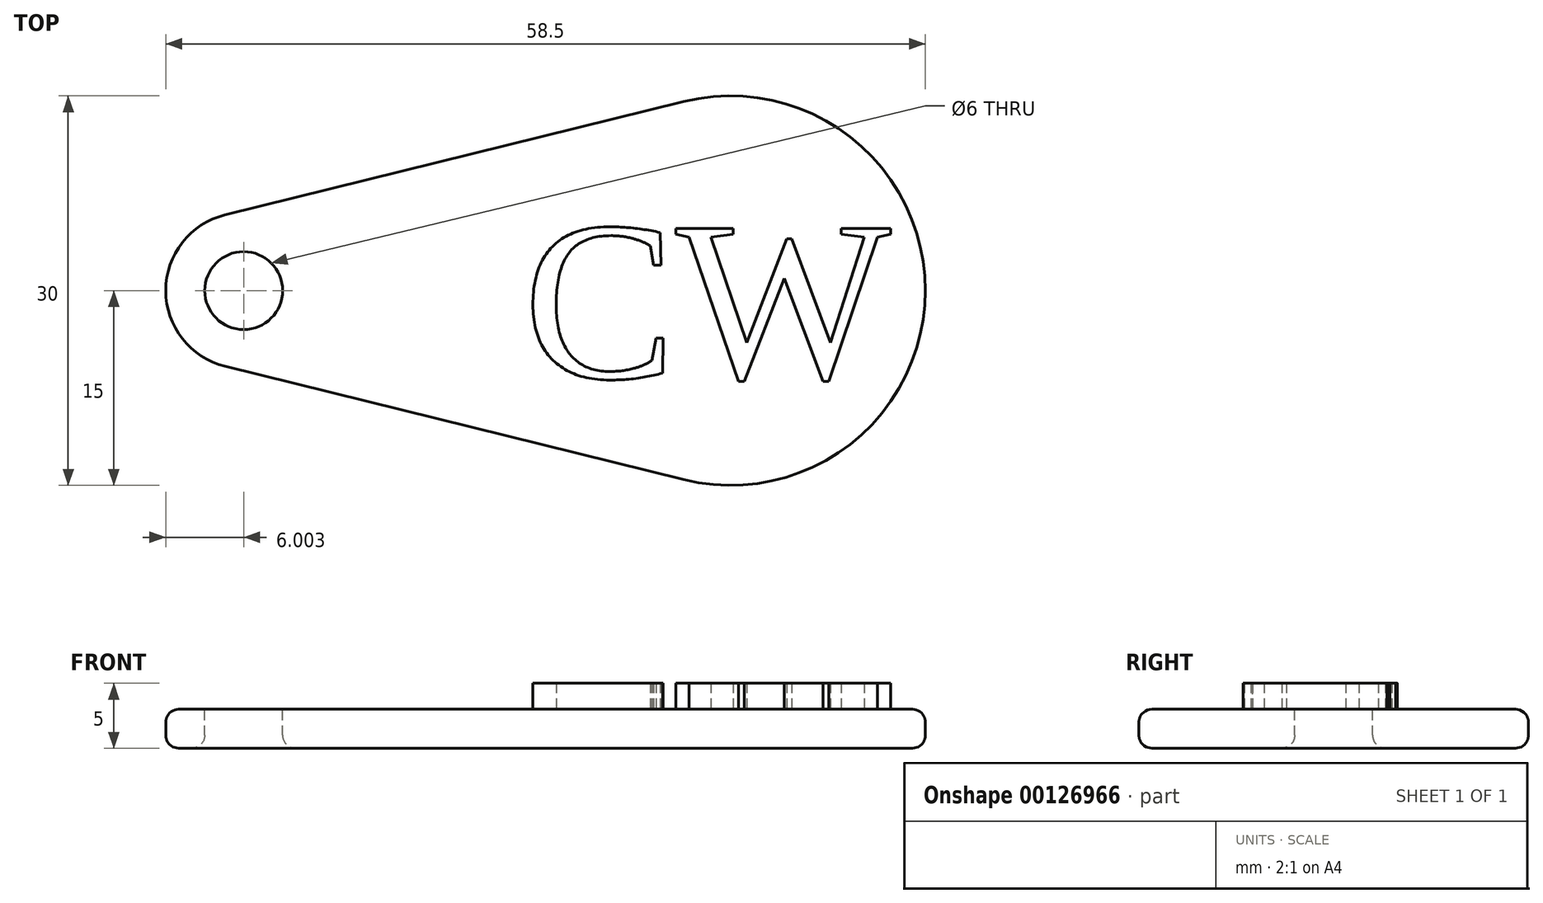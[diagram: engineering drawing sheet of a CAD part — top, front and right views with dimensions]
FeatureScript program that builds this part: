
annotation { "Feature Type Name" : "Feature", "Feature Type Description" : "" }
export const myFeature = defineFeature(function(context is Context, id is Id, definition is map)
    precondition{}
    {
        {
            var Q0;
            Q0=qCreatedBy(makeId("Top.planeOp"),FACE);
            var sketch = newSketch(context, id + "F0", { "sketchPlane" : qUnion([Q0])});
            skCircle(sketch, "E0", {"center": v(46.46, 0) * mm, "radius": 15 * mm});
            skCircle(sketch, "E1", {"center": v(8.96, 0) * mm, "radius": 6 * mm});
            skLineSegment(sketch, "E2", {"start": v(7.52, 5.82) * mm, "end": v(42.86, 14.56) * mm});
            skLineSegment(sketch, "E3", {"start": v(7.52, -5.82) * mm, "end": v(42.86, -14.56) * mm});
            skSolve(sketch);
        }
        {
            var Q0;
            {var subQ0=sQuery(id+"F0.wireOp",EDGE,"E1");var subQ1=makeQuery(id+"F0.imprint","INTERSECT",VERTEX,{"derivedFrom":[subQ0,sQuery(id+"F0.wireOp",EDGE,"E2")]});Q0=makeQuery(id+"F0.imprint","IMPRINT",FACE,{"disambiguationData":[TD([[makeQuery(id+"F0.imprint","IMPRINT",EDGE,{"disambiguationData":[TD([[subQ1,-1.0]])],"derivedFrom":subQ0}),1.0]])]});}
            var Q1;
            {var subQ0=sQuery(id+"F0.wireOp",EDGE,"E2");Q1=makeQuery(id+"F0.imprint","IMPRINT",FACE,{"disambiguationData":[TD([[makeQuery(id+"F0.imprint","IMPRINT",EDGE,{"derivedFrom":subQ0}),-1.0]])]});}
            var Q2;
            {var subQ0=sQuery(id+"F0.wireOp",EDGE,"E0");var subQ1=makeQuery(id+"F0.imprint","INTERSECT",VERTEX,{"derivedFrom":[subQ0,sQuery(id+"F0.wireOp",EDGE,"E2")]});Q2=makeQuery(id+"F0.imprint","IMPRINT",FACE,{"disambiguationData":[TD([[makeQuery(id+"F0.imprint","IMPRINT",EDGE,{"disambiguationData":[TD([[subQ1,-1.0]])],"derivedFrom":subQ0}),1.0]])]});}
            extrude(context, id + "F1", {"entities" : qUnion([Q0, Q1, Q2]), "depth" : 3 * mm});
        }
        {
            var Q0;
            Q0=makeQuery(id+"F1.opExtrude","CAP_FACE",FACE,{"disambiguationData":[OSD([sQuery(id+"F0.wireOp",EDGE,"E0"),sQuery(id+"F0.wireOp",EDGE,"E1"),sQuery(id+"F0.wireOp",EDGE,"E2"),sQuery(id+"F0.wireOp",EDGE,"E3")])],"isStart":false});
            var sketch = newSketch(context, id + "F2", { "sketchPlane" : qUnion([Q0])});
            skCircle(sketch, "E4", {"center": v(8.96, 0) * mm, "radius": 3 * mm});
            skSolve(sketch);
        }
        {
            var Q0;
            Q0=makeQuery(id+"F2.imprint","IMPRINT",FACE,{"disambiguationData":[TD([[makeQuery(id+"F2.imprint","IMPRINT",EDGE,{"derivedFrom":sQuery(id+"F2.wireOp",EDGE,"E4")}),1.0]])]});
            extrude(context, id + "F3", {"entities" : qUnion([Q0]), "operationType" : NewBodyOperationType.REMOVE, "oppositeDirection" : true, "depth" : 25 * mm});
        }
        {
            var Q0;
            Q0=makeQuery(id+"F1.opExtrude","CAP_FACE",FACE,{"disambiguationData":[OSD([sQuery(id+"F0.wireOp",EDGE,"E0"),sQuery(id+"F0.wireOp",EDGE,"E1"),sQuery(id+"F0.wireOp",EDGE,"E2"),sQuery(id+"F0.wireOp",EDGE,"E3")])],"isStart":false});
            var sketch = newSketch(context, id + "F4", { "sketchPlane" : qUnion([Q0])});
            skText(sketch, "E5", { "text": "CW", "fontName": "Tinos-Regular.ttf"});
            const initialGuessF4  = {"E5": [0.03052, -0.00672, 1, 0, 0.01265]};
            skSetInitialGuess(sketch, initialGuessF4);
            skSolve(sketch);
        }
        {
            var Q0;
            Q0 = qSketchRegion(id + "F4", true);
            extrude(context, id + "F5", {"entities" : qUnion([Q0]), "operationType" : NewBodyOperationType.ADD, "depth" : 2 * mm});
        }
        {
            var Q0;
            Q0=makeQuery(id+"F3.boolean.opBoolean","COPY",EDGE,{"derivedFrom":makeQuery(id+"F3.opExtrude","CAP_EDGE",EDGE,{"disambiguationData":[OSD([sQuery(id+"F2.wireOp",EDGE,"E4")])],"isStart":true})});
            var Q1;
            Q1=makeQuery(id+"F1.opExtrude","CAP_EDGE",EDGE,{"disambiguationData":[OSD([sQuery(id+"F0.wireOp",EDGE,"E3")])],"isStart":false});
            var Q2;
            Q2=makeQuery(id+"F1.opExtrude","CAP_EDGE",EDGE,{"disambiguationData":[OSD([sQuery(id+"F0.wireOp",EDGE,"E2")])],"isStart":true});
            var Q3;
            Q3=makeQuery(id+"F3.boolean.opBoolean","INTERSECT",EDGE,{"derivedFrom":[makeQuery(id+"F1.opExtrude","CAP_FACE",FACE,{"disambiguationData":[OSD([sQuery(id+"F0.wireOp",EDGE,"E0"),sQuery(id+"F0.wireOp",EDGE,"E1"),sQuery(id+"F0.wireOp",EDGE,"E2"),sQuery(id+"F0.wireOp",EDGE,"E3")])],"isStart":true}),makeQuery(id+"F3.opExtrude","SWEPT_FACE",FACE,{"disambiguationData":[OSD([sQuery(id+"F2.wireOp",EDGE,"E4")])]})]});
            fillet(context, id + "F6", {"entities" : qUnion([Q0, Q1, Q2, Q3]), "radius" : 1 * mm, "tangentPropagation" : true, "allowEdgeOverflow" : false});
        }
    });
